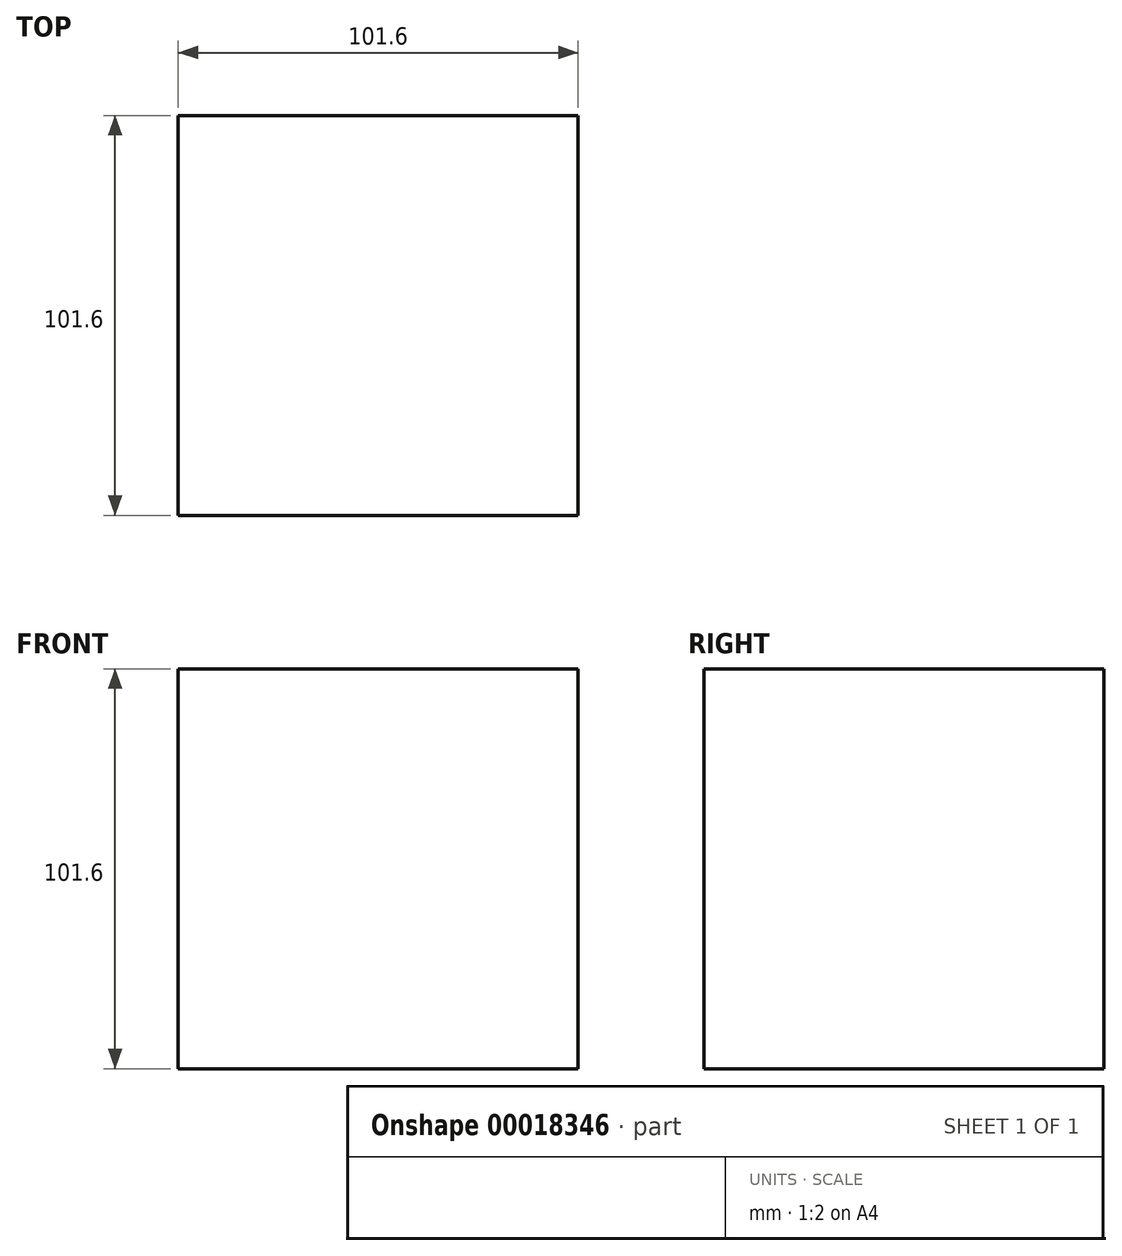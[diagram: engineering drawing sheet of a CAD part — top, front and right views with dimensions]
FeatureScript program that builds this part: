
annotation { "Feature Type Name" : "Feature", "Feature Type Description" : "" }
export const myFeature = defineFeature(function(context is Context, id is Id, definition is map)
    precondition{}
    {
        {
            var Q0;
            Q0=qCreatedBy(makeId("Front.planeOp"),FACE);
            var sketch = newSketch(context, id + "F0", { "sketchPlane" : qUnion([Q0])});
            skLineSegment(sketch, "E0.rect.bottom", {"start": v(-50.8, 50.8) * mm, "end": v(50.8, 50.8) * mm});
            skLineSegment(sketch, "E0.rect.top", {"start": v(-50.8, -50.8) * mm, "end": v(50.8, -50.8) * mm});
            skLineSegment(sketch, "E0.rect.left", {"start": v(-50.8, 50.8) * mm, "end": v(-50.8, -50.8) * mm});
            skLineSegment(sketch, "E0.rect.right", {"start": v(50.8, 50.8) * mm, "end": v(50.8, -50.8) * mm});
            skPoint(sketch, "E0.rect.middle", {"position": v(0, 0) * mm});
            skSolve(sketch);
        }
        {
            var Q0;
            Q0=makeQuery(id+"F0.imprint","IMPRINT",FACE,{"disambiguationData":[TD([[makeQuery(id+"F0.imprint","IMPRINT",EDGE,{"derivedFrom":sQuery(id+"F0.wireOp",EDGE,"E0.rect.bottom")}),-1.0]])]});
            extrude(context, id + "F1", {"entities" : qUnion([Q0]), "endBound" : BoundingType.SYMMETRIC, "depth" : 101.6 * mm});
        }
    });
